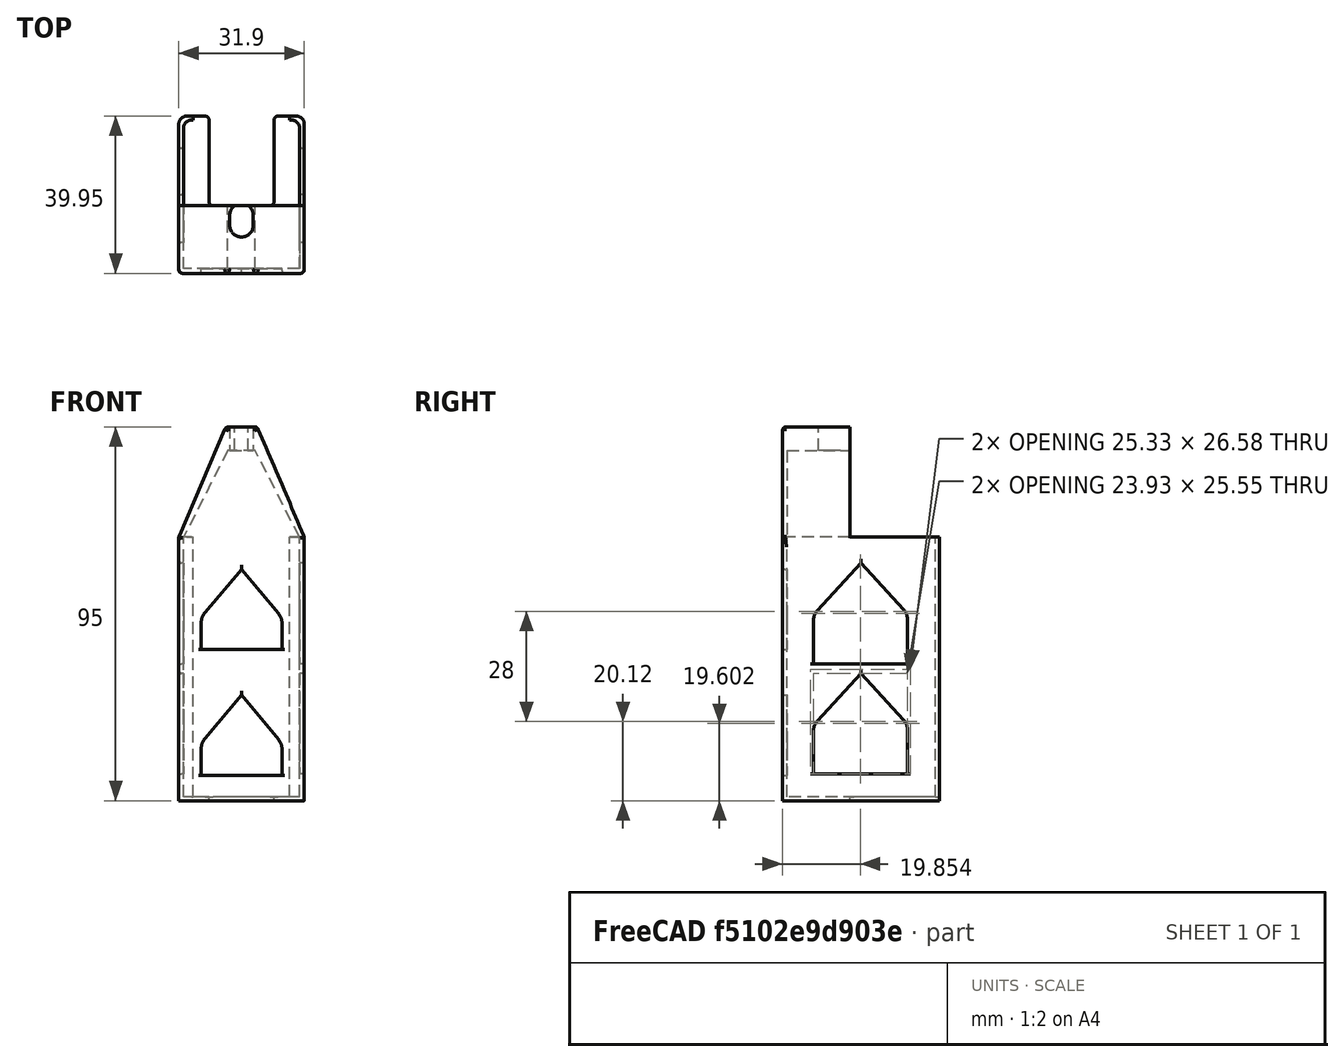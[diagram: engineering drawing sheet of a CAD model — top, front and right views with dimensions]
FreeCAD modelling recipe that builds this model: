
FCSTD DOCUMENT  (FreeCAD 0.19R)
Label: PlugTHing
License: All rights reserved
LicenseURL: http://en.wikipedia.org/wiki/All_rights_reserved
objects: PartDesign::Fillet×9, Sketcher::SketchObject×8, PartDesign::Pad×4, PartDesign::Pocket×4, PartDesign::LinearPattern×2, PartDesign::Body×1, Mesh::Feature×1
note: 45 computed .brp shape members not serialized (recipe doc carries the construction recipe); baked Part::Feature solids carry a one-line shape summary decoded from their .brp

FEATURE [Sketcher::SketchObject] Sketch
  FullyConstrained = true
  MapMode = 5
  Support = -> [XY_Plane]
  sketch-geometry (12):
    g0: LineSegment StartX=14.75 StartY=37.75 StartZ=0 EndX=14.75 EndY=0 EndZ=0
    g1: LineSegment StartX=14.75 StartY=0 StartZ=0 EndX=-14.75 EndY=0 EndZ=0
    g2: LineSegment StartX=-14.75 StartY=0 StartZ=0 EndX=-14.75 EndY=37.75 EndZ=0
    g3: LineSegment StartX=14.75 StartY=37.75 StartZ=0 EndX=12.25 EndY=37.75 EndZ=0
    g4: LineSegment StartX=-14.75 StartY=37.75 StartZ=0 EndX=-12.25 EndY=37.75 EndZ=0
    g5: LineSegment StartX=12.25 StartY=37.75 StartZ=0 EndX=12.25 EndY=38.75 EndZ=0
    g6: LineSegment StartX=12.25 StartY=38.75 StartZ=0 EndX=15.95 EndY=38.75 EndZ=0
    g7: LineSegment StartX=15.95 StartY=38.75 StartZ=0 EndX=15.95 EndY=-1.2 EndZ=0
    g8: LineSegment StartX=15.95 StartY=-1.2 StartZ=0 EndX=-15.95 EndY=-1.2 EndZ=0
    g9: LineSegment StartX=-15.95 StartY=-1.2 StartZ=0 EndX=-15.95 EndY=38.75 EndZ=0
    g10: LineSegment StartX=-15.95 StartY=38.75 StartZ=0 EndX=-12.25 EndY=38.75 EndZ=0
    g11: LineSegment StartX=-12.25 StartY=38.75 StartZ=0 EndX=-12.25 EndY=37.75 EndZ=0
  constraints (35):
    c: Coincident(g0,g1)
    c: Coincident(g1,g2)
    c: Horizontal(g1)
    c: Vertical(g0)
    c: Vertical(g2)
    c: Symmetric(g0,g1,g-1)
    c: Distance(g1) = 29.5
    c: Distance(g0) = 37.75
    c: Coincident(g3,g0)
    c: Coincident(g4,g2)
    c: Horizontal(g4)
    c: Coincident(g5,g3)
    c: Coincident(g5,g6)
    c: Coincident(g6,g7)
    c: Vertical(g7)
    c: Coincident(g7,g8)
    c: Horizontal(g8)
    c: Coincident(g8,g9)
    c: Vertical(g9)
    c: Coincident(g9,g10)
    c: Horizontal(g10)
    c: Coincident(g10,g11)
    c: Coincident(g11,g4)
    c: Distance(g1,g9) = 1.2
    c: Distance(g7,g0) = 1.2
    c: Distance(g7,g1) = 1.2
    c: Distance(g2,g10) = 1
    c: Distance(g0,g6) = 1
    c: Horizontal(g6)
    c: Horizontal(g3)
    c: Vertical(g11)
    c: DistanceY(g2) = 37.75
    c: Distance(g4) = 2.5
    c: Equal(g3,g4)
    c: Vertical(g5)
FEATURE [PartDesign::Pad] Pad
  Direction = (1,1,1)
  Length = 66
  Length2 = 100
  Profile = -> Sketch
  Type = 0
FEATURE [Sketcher::SketchObject] Sketch001
  ExternalGeometry = -> [Pad]
  FullyConstrained = true
  MapMode = 5
  Placement = pos=(0,0,0) rot=(1,0,0;3.14159rad)
  Support = -> [Pad]
  sketch-geometry (4):
    g0: LineSegment StartX=-15.95 StartY=1.2 StartZ=0 EndX=15.95 EndY=1.2 EndZ=0
    g1: LineSegment StartX=15.95 StartY=1.2 StartZ=0 EndX=15.95 EndY=-38.75 EndZ=0
    g2: LineSegment StartX=15.95 StartY=-38.75 StartZ=0 EndX=-15.95 EndY=-38.75 EndZ=0
    g3: LineSegment StartX=-15.95 StartY=-38.75 StartZ=0 EndX=-15.95 EndY=1.2 EndZ=0
  constraints (9):
    c: Coincident(g0,g1)
    c: Coincident(g1,g2)
    c: Coincident(g2,g3)
    c: Coincident(g3,g0)
    c: Horizontal(g2)
    c: Vertical(g3)
    c: Coincident(g0,g-3)
    c: Coincident(g0,g-3)
    c: Coincident(g1,g-4)
FEATURE [PartDesign::Pad] Pad001
  BaseFeature = -> Pad
  Direction = (1,1,1)
  Length = 1
  Length2 = 100
  Profile = -> Sketch001
  Type = 0
FEATURE [Sketcher::SketchObject] Sketch002
  ExternalGeometry = -> [Pad001]
  FullyConstrained = true
  MapMode = 5
  Placement = pos=(0,-1.2,0) rot=(1,0,0;1.5708rad)
  Support = -> [Pad001]
  sketch-geometry (4):
    g0: LineSegment StartX=-15.95 StartY=66 StartZ=0 EndX=-4 EndY=94 EndZ=0
    g1: LineSegment StartX=-4 StartY=94 StartZ=0 EndX=4 EndY=94 EndZ=0
    g2: LineSegment StartX=4 StartY=94 StartZ=0 EndX=15.95 EndY=66 EndZ=0
    g3: LineSegment StartX=15.95 StartY=66 StartZ=0 EndX=-15.95 EndY=66 EndZ=0
  constraints (9):
    c: Coincident(g-3,g0)
    c: Coincident(g0,g1)
    c: Coincident(g1,g2)
    c: Coincident(g2,g-3)
    c: Coincident(g2,g3)
    c: Coincident(g3,g0)
    c: Distance(g1) = 8
    c: Symmetric(g1,g0,g-2)
    c: Distance(g1,g3) = 28
FEATURE [PartDesign::Pad] Pad002
  BaseFeature = -> Pad001
  Direction = (1,1,1)
  Length = 1.2
  Length2 = 100
  Profile = -> Sketch002
  Reversed = true
  Type = 0
FEATURE [Sketcher::SketchObject] Sketch007
  ExternalGeometry = -> [Pad002]
  FullyConstrained = true
  MapMode = 5
  Placement = pos=(0,-2.6e-15,0) rot=(0,0.707107,0.707107;3.14159rad)
  Support = -> [Pad002]
  sketch-geometry (8):
    g0: LineSegment StartX=-15.95 StartY=66 StartZ=0 EndX=-14.7 EndY=66 EndZ=0
    g1: LineSegment StartX=-14.7 StartY=66 StartZ=0 EndX=-3.5 EndY=88 EndZ=0
    g2: LineSegment StartX=-3.5 StartY=88 StartZ=0 EndX=3.5 EndY=88 EndZ=0
    g3: LineSegment StartX=3.5 StartY=88 StartZ=0 EndX=14.7 EndY=66 EndZ=0
    g4: LineSegment StartX=14.7 StartY=66 StartZ=0 EndX=15.95 EndY=66 EndZ=0
    g5: LineSegment StartX=15.95 StartY=66 StartZ=0 EndX=4 EndY=94 EndZ=0
    g6: LineSegment StartX=4 StartY=94 StartZ=0 EndX=-4 EndY=94 EndZ=0
    g7: LineSegment StartX=-4 StartY=94 StartZ=0 EndX=-15.95 EndY=66 EndZ=0
  constraints (19):
    c: Coincident(g4,g3)
    c: Distance(g4) = 1.25
    c: Coincident(g4,g5)
    c: Distance(g0) = 1.25
    c: Coincident(g0,g7)
    c: Coincident(g1,g0)
    c: Coincident(g0,g-4)
    c: Horizontal(g0)
    c: Horizontal(g4)
    c: Coincident(g4,g-3)
    c: Distance(g2) = 7
    c: Symmetric(g2,g2,g-2)
    c: Coincident(g3,g2)
    c: Coincident(g1,g2)
    c: DistanceY(g2) = 88
    c: Coincident(g7,g-4)
    c: Coincident(g6,g7)
    c: Coincident(g6,g-3)
    c: Coincident(g5,g6)
FEATURE [PartDesign::Pad] Pad003
  BaseFeature = -> Pad002
  Direction = (1,1,1)
  Length = 16
  Length2 = 100
  Profile = -> Sketch007
  Type = 0
FEATURE [Sketcher::SketchObject] Sketch011
  FullyConstrained = false
  MapMode = 5
  Placement = pos=(0,0,-1) rot=(1,0,0;3.14159rad)
  Support = -> [Pad003]
  sketch-geometry (4):
    g0: LineSegment StartX=-8.23572 StartY=-16 StartZ=0 EndX=8.23572 EndY=-16 EndZ=0
    g1: LineSegment StartX=8.23572 StartY=-16 StartZ=0 EndX=8.23572 EndY=-46.4155 EndZ=0
    g2: LineSegment StartX=8.23572 StartY=-46.4155 StartZ=0 EndX=-8.23572 EndY=-46.4155 EndZ=0
    g3: LineSegment StartX=-8.23572 StartY=-46.4155 StartZ=0 EndX=-8.23572 EndY=-16 EndZ=0
  constraints (9):
    c: Coincident(g0,g1)
    c: Coincident(g1,g2)
    c: Coincident(g2,g3)
    c: Coincident(g3,g0)
    c: Horizontal(g2)
    c: Vertical(g1)
    c: Vertical(g3)
    c: Symmetric(g0,g0,g-2)
    c: DistanceY(g0) = -16
FEATURE [PartDesign::Pocket] Pocket
  BaseFeature = -> Pad003
  Length = 5
  Length2 = 100
  Profile = -> Sketch011
  Type = 0
FEATURE [Sketcher::SketchObject] Sketch012
  FullyConstrained = false
  MapMode = 5
  Placement = pos=(0,2.09e-14,94) rot=(0,0,1;0rad)
  Support = -> [Pocket]
  sketch-geometry (4):
    g0: ArcOfCircle CenterX=-0.014618 CenterY=13.549 CenterZ=0 NormalX=0 NormalY=0 NormalZ=1 AngleXU=0 Radius=3 StartAngle=0 EndAngle=3.14159
    g1: ArcOfCircle CenterX=-0.014618 CenterY=11.034 CenterZ=0 NormalX=0 NormalY=0 NormalZ=1 AngleXU=0 Radius=3 StartAngle=3.14159 EndAngle=6.28319
    g2: LineSegment StartX=-3.01462 StartY=13.549 StartZ=0 EndX=-3.01462 EndY=11.034 EndZ=0
    g3: LineSegment StartX=2.98538 StartY=13.549 StartZ=0 EndX=2.98538 EndY=11.034 EndZ=0
  constraints (7):
    c: Tangent(g0,g3) = 1.5708
    c: Tangent(g0,g2) = -1.5708
    c: Tangent(g2,g1) = -1.5708
    c: Tangent(g3,g1) = 1.5708
    c: Vertical(g2)
    c: Equal(g0,g1)
    c: Radius(g1) = 3
FEATURE [PartDesign::Pocket] Pocket001
  BaseFeature = -> Pocket
  Length = 8
  Length2 = 100
  Profile = -> Sketch012
  Type = 0
FEATURE [Sketcher::SketchObject] Sketch014
  FullyConstrained = false
  MapMode = 5
  Placement = pos=(0,-1.2,0) rot=(1,0,0;1.5708rad)
  Support = -> [Pocket001]
  sketch-geometry (5):
    g0: LineSegment StartX=0 StartY=25.8332 StartZ=0 EndX=-10.2379 EndY=13.7475 EndZ=0
    g1: LineSegment StartX=-10.2379 StartY=13.7475 StartZ=0 EndX=-10.2379 EndY=5.43468 EndZ=0
    g2: LineSegment StartX=-10.2379 StartY=5.43468 StartZ=0 EndX=10.2979 EndY=5.43468 EndZ=0
    g3: LineSegment StartX=10.2979 StartY=5.43468 StartZ=0 EndX=10.2979 EndY=13.4432 EndZ=0
    g4: LineSegment StartX=10.2979 StartY=13.4432 StartZ=0 EndX=0 EndY=25.8332 EndZ=0
  constraints (10):
    c: PointOnObject(g0,g-2)
    c: Coincident(g0,g1)
    c: Vertical(g1)
    c: Coincident(g1,g2)
    c: Horizontal(g2)
    c: Coincident(g2,g3)
    c: Coincident(g3,g4)
    c: Coincident(g4,g0)
    c: Vertical(g3)
    c: Angle(g0,g4) = 1.39626
FEATURE [PartDesign::Pocket] Pocket002
  BaseFeature = -> Pocket001
  Length = 5
  Length2 = 100
  Profile = -> Sketch014
  Type = 0
FEATURE [PartDesign::LinearPattern] LinearPattern
  BaseFeature = -> Pocket002
  Direction = -> Sketch014 [V_Axis]
  Length = 32
  Occurrences = 2
  Originals = -> [Pocket002]
FEATURE [Sketcher::SketchObject] Sketch015
  FullyConstrained = false
  MapMode = 5
  Placement = pos=(15.95,0,0) rot=(0.57735,0.57735,0.57735;2.0944rad)
  Support = -> [LinearPattern]
  sketch-geometry (5):
    g0: LineSegment StartX=18.7701 StartY=31.3746 StartZ=0 EndX=6.68775 EndY=18.189 EndZ=0
    g1: LineSegment StartX=6.68775 StartY=18.189 StartZ=0 EndX=6.68775 EndY=5.82921 EndZ=0
    g2: LineSegment StartX=6.68775 StartY=5.82921 StartZ=0 EndX=30.6205 EndY=5.82921 EndZ=0
    g3: LineSegment StartX=30.6205 StartY=5.82921 StartZ=0 EndX=30.6205 EndY=18.4421 EndZ=0
    g4: LineSegment StartX=30.6205 StartY=18.4421 StartZ=0 EndX=18.7701 EndY=31.3746 EndZ=0
  constraints (10):
    c: Coincident(g0,g1)
    c: Vertical(g1)
    c: Coincident(g1,g2)
    c: Horizontal(g2)
    c: Coincident(g2,g3)
    c: Coincident(g3,g4)
    c: Coincident(g4,g0)
    c: Angle(g0,g4) = 1.48353
    c: Vertical(g3)
    c: Angle(g0) = -2.31256
FEATURE [PartDesign::Pocket] Pocket003
  BaseFeature = -> LinearPattern
  Length = 5
  Length2 = 100
  Profile = -> Sketch015
  Type = 1
FEATURE [PartDesign::LinearPattern] LinearPattern001
  BaseFeature = -> Pocket003
  Direction = -> Sketch015 [V_Axis]
  Length = 28
  Occurrences = 2
  Originals = -> [Pocket003]
FEATURE [PartDesign::Fillet] Fillet
  Base = -> LinearPattern001 [Edge96,Edge87,Edge94,Edge92]
  BaseFeature = -> LinearPattern001
  Radius = 1
  SupportTransform = false
FEATURE [PartDesign::Fillet] Fillet001
  Base = -> Fillet [Edge28,Edge63]
  BaseFeature = -> Fillet
  Radius = 2
  SupportTransform = false
FEATURE [PartDesign::Fillet] Fillet002
  Base = -> Fillet001 [Edge96,Edge172]
  BaseFeature = -> Fillet001
  Radius = 2
  SupportTransform = false
FEATURE [PartDesign::Fillet] Fillet003
  Base = -> Fillet002 [Edge199,Edge223]
  BaseFeature = -> Fillet002
  Radius = 1
  SupportTransform = false
FEATURE [PartDesign::Fillet] Fillet004
  Base = -> Fillet003 [Edge44,Edge134]
  BaseFeature = -> Fillet003
  Radius = 1
  SupportTransform = false
FEATURE [PartDesign::Fillet] Fillet005
  Base = -> Fillet004 [Edge214,Edge224,Edge83,Edge73,Edge76,Edge88,Edge228,Edge221,Edge144,Edge154,Edge151,Edge158]
  BaseFeature = -> Fillet004
  Radius = 4
  SupportTransform = false
FEATURE [PartDesign::Fillet] Fillet006
  Base = -> Fillet005 [Edge8]
  BaseFeature = -> Fillet005
  Radius = 1
  SupportTransform = false
FEATURE [PartDesign::Fillet] Fillet007
  Base = -> Fillet006 [Edge101]
  BaseFeature = -> Fillet006
  Radius = 1
  SupportTransform = false
FEATURE [PartDesign::Fillet] Fillet008
  Base = -> Fillet007 [Edge108,Edge106,Edge113,Edge115,Edge70,Edge68,Edge61,Edge63,Edge88,Edge95,Edge93,Edge86]
  BaseFeature = -> Fillet007
  Radius = 0.7
  SupportTransform = false
FEATURE [PartDesign::Body] Body
  Group = -> [Sketch,Pad,Sketch001,Pad001,Sketch002,Pad002,Sketch007,Pad003,Sketch011,Pocket,Sketch012,Pocket001,Sketch014,Pocket002,LinearPattern,Sketch015,Pocket003,LinearPattern001,Fillet,Fillet001,Fillet002,Fillet003,Fillet004,Fillet005,Fillet006,Fillet007,Fillet008]
  Origin = -> Origin
  Tip = -> Fillet008
FEATURE [Mesh::Feature] Mesh  label="Fillet008 (Meshed)"
